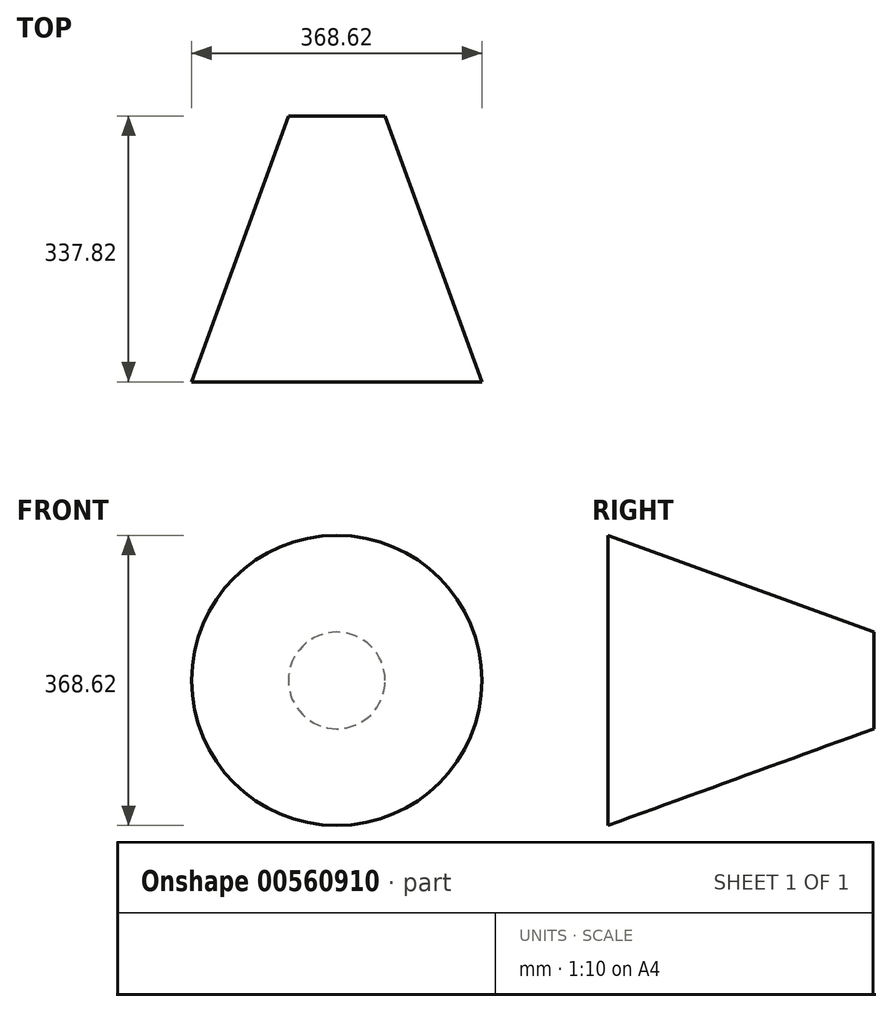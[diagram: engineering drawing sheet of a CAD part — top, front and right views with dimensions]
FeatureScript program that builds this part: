
annotation { "Feature Type Name" : "Feature", "Feature Type Description" : "" }
export const myFeature = defineFeature(function(context is Context, id is Id, definition is map)
    precondition{}
    {
        {
            var Q0;
            Q0=qCreatedBy(makeId("Front.planeOp"),FACE);
            var sketch = newSketch(context, id + "F0", { "sketchPlane" : qUnion([Q0])});
            skCircle(sketch, "E0", {"center": v(0, 0) * mm, "radius": 61.35 * mm});
            skSolve(sketch);
        }
        {
            var Q0;
            Q0=makeQuery(id+"F0.imprint","IMPRINT",FACE,{"disambiguationData":[TD([[makeQuery(id+"F0.imprint","IMPRINT",EDGE,{"derivedFrom":sQuery(id+"F0.wireOp",EDGE,"E0")}),1.0]])]});
            extrude(context, id + "F1", {"entities" : qUnion([Q0]), "depth" : 337.82 * mm, "offsetDistance" : 25.4 * mm, "hasDraft" : true, "draftAngle" : 20 * degree});
        }
    });
